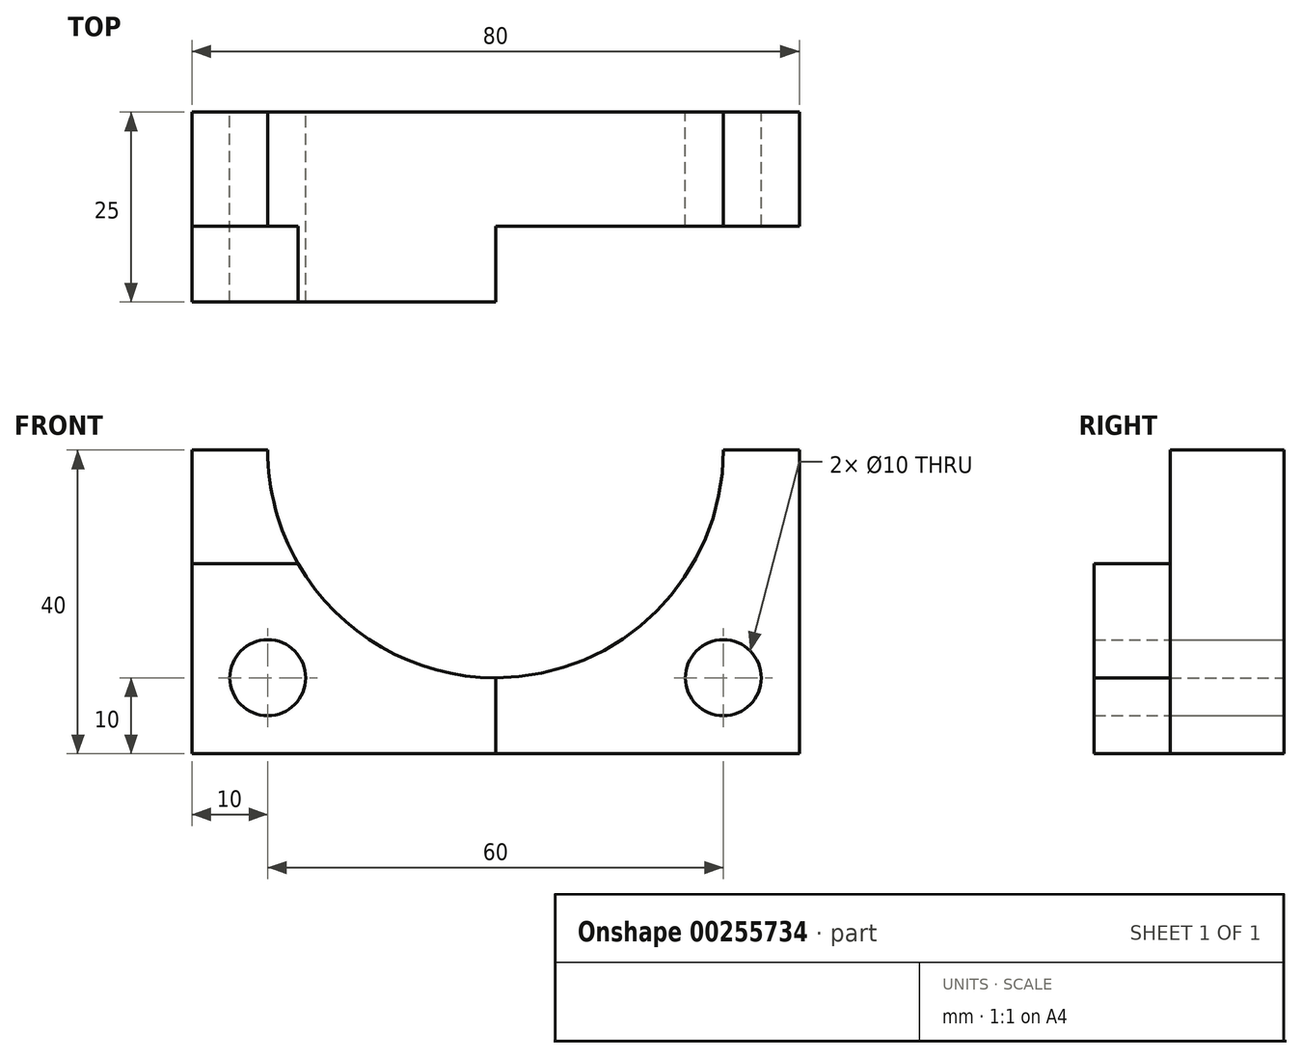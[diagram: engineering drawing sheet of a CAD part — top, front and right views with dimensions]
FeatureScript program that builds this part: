
annotation { "Feature Type Name" : "Feature", "Feature Type Description" : "" }
export const myFeature = defineFeature(function(context is Context, id is Id, definition is map)
    precondition{}
    {
        {
            var Q0;
            Q0=qCreatedBy(makeId("Front.planeOp"),FACE);
            var sketch = newSketch(context, id + "F0", { "sketchPlane" : qUnion([Q0])});
            skLineSegment(sketch, "E0.bottom", {"start": v(-40, 40) * mm, "end": v(-30, 40) * mm});
            skLineSegment(sketch, "E0.top", {"start": v(-40, 0) * mm, "end": v(40, 0) * mm});
            skLineSegment(sketch, "E0.left", {"start": v(-40, 40) * mm, "end": v(-40, 0) * mm});
            skLineSegment(sketch, "E0.right", {"start": v(40, 40) * mm, "end": v(40, 0) * mm});
            skArc(sketch, "E1", {"start": v(-30, 40) * mm, "mid": v(0, 10) * mm, "end": v(30, 40) * mm});
            skCircle(sketch, "E2", {"center": v(-30, 10) * mm, "radius": 5 * mm});
            skCircle(sketch, "E3", {"center": v(30, 10) * mm, "radius": 5 * mm});
            skLineSegment(sketch, "E4.trimOffspring", {"start": v(30, 40) * mm, "end": v(40, 40) * mm});
            skSolve(sketch);
        }
        {
            var Q0;
            Q0=makeQuery(id+"F0.imprint","IMPRINT",FACE,{"disambiguationData":[TD([[makeQuery(id+"F0.imprint","IMPRINT",EDGE,{"derivedFrom":sQuery(id+"F0.wireOp",EDGE,"E0.bottom")}),-1.0]])]});
            extrude(context, id + "F1", {"entities" : qUnion([Q0]), "depth" : 25 * mm});
        }
        {
            var Q0;
            Q0=makeQuery(id+"F1.opExtrude","CAP_FACE",FACE,{"disambiguationData":[OSD([sQuery(id+"F0.wireOp",EDGE,"E0.bottom"),sQuery(id+"F0.wireOp",EDGE,"E0.top"),sQuery(id+"F0.wireOp",EDGE,"E0.left"),sQuery(id+"F0.wireOp",EDGE,"E0.right"),sQuery(id+"F0.wireOp",EDGE,"E1"),sQuery(id+"F0.wireOp",EDGE,"E2"),sQuery(id+"F0.wireOp",EDGE,"E3"),sQuery(id+"F0.wireOp",EDGE,"E4.trimOffspring")])],"isStart":false});
            var sketch = newSketch(context, id + "F2", { "sketchPlane" : qUnion([Q0])});
            skLineSegment(sketch, "E5.bottom", {"start": v(-45.65, 42.5) * mm, "end": v(-15.62, 42.5) * mm});
            skLineSegment(sketch, "E5.top", {"start": v(-45.65, 25) * mm, "end": v(-15.62, 25) * mm});
            skLineSegment(sketch, "E5.left", {"start": v(-45.65, 42.5) * mm, "end": v(-45.65, 25) * mm});
            skLineSegment(sketch, "E5.right", {"start": v(-15.62, 42.5) * mm, "end": v(-15.62, 25) * mm});
            skLineSegment(sketch, "E6.bottom", {"start": v(0, 43.91) * mm, "end": v(51.29, 43.91) * mm});
            skLineSegment(sketch, "E6.top", {"start": v(0, -15.43) * mm, "end": v(51.29, -15.43) * mm});
            skLineSegment(sketch, "E6.left", {"start": v(0, 43.91) * mm, "end": v(0, -15.43) * mm});
            skLineSegment(sketch, "E6.right", {"start": v(51.29, 43.91) * mm, "end": v(51.29, -15.43) * mm});
            skSolve(sketch);
        }
        {
            var Q0;
            {var subQ5=makeQuery(id+"F1.opExtrude","CAP_EDGE",EDGE,{"disambiguationData":[OSD([sQuery(id+"F0.wireOp",EDGE,"E0.bottom")])],"isStart":false});Q0=makeQuery(id+"F2.imprint","IMPRINT",FACE,{"disambiguationData":[TD([[makeQuery(id+"F2.imprint","IMPRINT",EDGE,{"derivedFrom":subQ5}),-1.0]])]});}
            var Q1;
            {var subQ0=makeQuery(id+"F1.opExtrude","CAP_EDGE",EDGE,{"disambiguationData":[OSD([sQuery(id+"F0.wireOp",EDGE,"E0.right")])],"isStart":false});Q1=makeQuery(id+"F2.imprint","IMPRINT",FACE,{"disambiguationData":[TD([[makeQuery(id+"F2.imprint","IMPRINT",EDGE,{"derivedFrom":subQ0}),-1.0]])]});}
            extrude(context, id + "F3", {"entities" : qUnion([Q0, Q1]), "operationType" : NewBodyOperationType.REMOVE, "oppositeDirection" : true, "depth" : 10 * mm});
        }
    });
